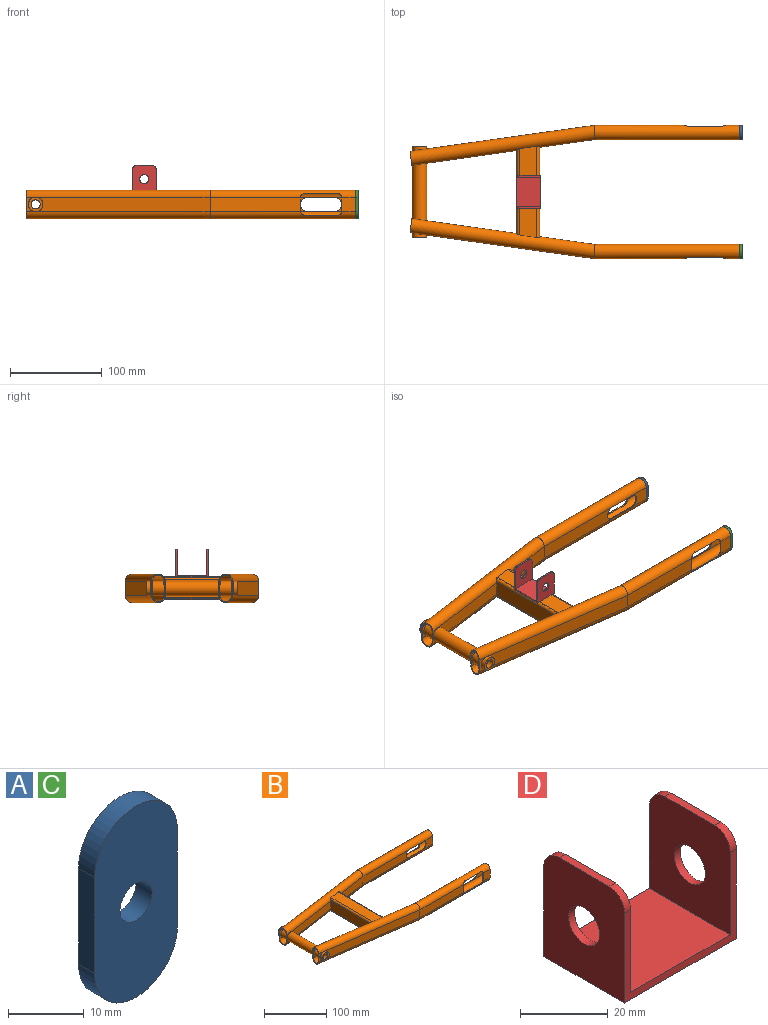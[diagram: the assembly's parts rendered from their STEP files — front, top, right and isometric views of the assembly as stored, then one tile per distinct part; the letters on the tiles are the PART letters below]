
ASSEMBLY  parts=4 mates=3
PART A: 7 faces, bbox 15.5x3x31 mm
  f0: cylinder r=7.75mm len=15.5mm, axis (0,1,0), area 73mm2, adj f1,f3,f4,f5
  f1: plane 15.5x3mm, normal (-1,0,0), area 46.5mm2, adj f0,f2,f4,f5
  f2: cylinder r=7.75mm len=15.5mm, axis (0,1,0), area 73mm2, adj f1,f3,f4,f5
  f3: plane 15.5x3mm, normal (1,0,0), area 46.5mm2, adj f0,f2,f4,f5
  f4: plane 31x15.5mm, normal (0,-1,0), area 400.7mm2, adj f0,f1,f2,f3,f6
  f5: plane 31x15.5mm, normal (0,1,0), area 400.7mm2, adj f0,f1,f2,f3,f6
  f6: cylinder r=3mm len=6mm, axis (0,-1,0), area 56.5mm2, adj f4,f5
PART B: 107 faces, bbox 359.6x145.6x31.1 mm
  f0: plane 60.41x15.5mm, normal (0.14,-0.99,0), area 945.6mm2, adj f2,f3,f19,f93
  f1: plane 60.41x15.5mm, normal (0.14,0.99,0), area 945.6mm2, adj f4,f66,f80,f93
  f2: cylinder r=7.75mm len=203.08mm, axis (-0.99,-0.14,0), area 4801.1mm2, adj f0,f5,f6,f16,f17,f20,f22,f82
  f3: cylinder r=7.75mm len=203.08mm, axis (-0.99,-0.14,0), area 4801.1mm2, adj f0,f5,f6,f16,f17,f18,f22,f82
  f4: cylinder r=7.75mm len=203.08mm, axis (-0.99,0.14,0), area 4801.1mm2, adj f1,f42,f63,f67,f68,f69,f79,f81
  f5: plane 15.5x8.5mm, normal (-0.14,0.99,0), area 63.2mm2, adj f2,f3,f22,f83
  f6: plane 15.5x6.34mm, normal (0.14,-0.99,0), area 29.4mm2, adj f2,f3,f22,f82
  f7: cylinder r=6.55mm len=202.67mm, axis (-0.99,-0.14,0), area 4162.7mm2, adj f8,f10,f22,f24,f25,f28,f41
  f8: plane 15.5x8.33mm, normal (0.14,-0.99,0), area 60.6mm2, adj f7,f9,f22,f41
  f9: cylinder r=6.55mm len=202.67mm, axis (-0.99,-0.14,0), area 4162.7mm2, adj f8,f10,f22,f24,f25,f26,f41
  f10: plane 15.5x6.51mm, normal (-0.14,0.99,0), area 32mm2, adj f7,f9,f22,f41
  f11: plane 15.5x14.85mm, normal (0,1,0), area 229.3mm2, adj f18,f20,f23,f33,f34,f35
  f12: plane 15.5x14.85mm, normal (0,-1,0), area 229.3mm2, adj f23,f26,f28,f33,f34,f35
  f13: plane 22.54x15.5mm, normal (0,-1,0), area 255mm2, adj f18,f20,f23,f29
  f14: plane 22.54x15.5mm, normal (0,1,0), area 255mm2, adj f23,f26,f28,f29
  f15: plane 105.53x15.5mm, normal (0,1,0), area 1541.4mm2, adj f25,f26,f28,f31
  f16: plane 188.46x26.49mm, normal (-0.14,0.99,0), area 2880.1mm2, adj f2,f3,f21,f83
  f17: plane 104.13x15.5mm, normal (0.14,-0.99,0), area 1560.1mm2, adj f2,f3,f82,f92
  f18: cylinder r=7.75mm len=158.57mm, axis (-1,0,0), area 3657mm2, adj f3,f11,f13,f19,f21,f23,f30,f33
  f19: plane 105.45x15.5mm, normal (0,-1,0), area 1540.1mm2, adj f0,f18,f20,f31
  f20: cylinder r=7.75mm len=158.57mm, axis (-1,0,0), area 3657mm2, adj f2,f11,f13,f19,f21,f23,f32,f35
  f21: plane 98.84x15.5mm, normal (0,1,0), area 1531.1mm2, adj f16,f18,f20,f37,f38,f39
  f22: plane 31x15.35mm, normal (-0.99,-0.14,0), area 91.1mm2, adj f2,f3,f5,f6,f7,f8,f9,f10
  f23: plane 31x15.5mm, normal (1,0,0), area 91.1mm2, adj f11,f12,f13,f14,f18,f20,f26,f28
  f24: plane 188.55x26.5mm, normal (0.14,-0.99,0), area 2881.4mm2, adj f7,f9,f27,f41
  f25: plane 189.46x26.63mm, normal (-0.14,0.99,0), area 2895.7mm2, adj f7,f9,f15,f41
  f26: cylinder r=6.55mm len=158.49mm, axis (-1,0,0), area 3056.2mm2, adj f9,f12,f14,f15,f23,f27,f30,f33
  f27: plane 98.75x15.5mm, normal (0,-1,0), area 1529.8mm2, adj f24,f26,f28,f37,f38,f39
  f28: cylinder r=6.55mm len=158.49mm, axis (-1,0,0), area 3056.2mm2, adj f7,f12,f14,f15,f23,f27,f32,f35
  f29: cylinder r=7.75mm len=15.5mm, axis (0,-1,0), area 29.2mm2, adj f13,f14,f30,f32
  f30: plane 29.5x1.2mm, normal (0,0,-1), area 35.4mm2, adj f18,f26,f29,f31
  f31: cylinder r=7.75mm len=15.5mm, axis (0,-1,0), area 29.2mm2, adj f15,f19,f30,f32
  f32: plane 29.5x1.2mm, normal (0,0,1), area 35.4mm2, adj f20,f28,f29,f31
  f33: cylinder r=5mm len=5mm, axis (0,1,0), area 10.4mm2, adj f11,f12,f18,f26,f34,f40
  f34: plane 14x1.2mm, normal (-1,0,0), area 16.8mm2, adj f11,f12,f33,f35
  f35: cylinder r=5mm len=5mm, axis (0,1,0), area 10.4mm2, adj f11,f12,f20,f28,f34,f36
  f36: plane 35x1.5mm, normal (0,0,1), area 52.4mm2, adj f20,f28,f35,f37
  f37: cylinder r=5mm len=5mm, axis (0,1,0), area 10.4mm2, adj f20,f21,f27,f28,f36,f38
  f38: plane 14x1.2mm, normal (1,0,0), area 16.8mm2, adj f21,f27,f37,f39
  f39: cylinder r=5mm len=5mm, axis (0,1,0), area 10.4mm2, adj f18,f21,f26,f27,f38,f40
  f40: plane 35x1.5mm, normal (0,0,-1), area 52.4mm2, adj f18,f26,f33,f39
  f41: cylinder r=8mm len=16mm, axis (0,1,0), area 664.9mm2, adj f7,f8,f9,f10,f24,f25
  f42: cylinder r=8mm len=16mm, axis (0,1,0), area 201.8mm2, adj f4,f43,f69,f80,f81
  f43: plane 16x16mm, normal (0,-1,0), area 122.5mm2, adj f42,f85
  f44: cylinder r=8mm len=16mm, axis (0,1,0), area 664.9mm2, adj f60,f61,f75,f76,f77,f78
  f45: plane 35x1.5mm, normal (0,0,-1), area 52.4mm2, adj f46,f52,f59,f67
  f46: cylinder r=5mm len=5mm, axis (0,-1,0), area 10.4mm2, adj f45,f47,f58,f59,f64,f67
  f47: plane 14x1.2mm, normal (1,0,0), area 16.8mm2, adj f46,f48,f58,f64
  f48: cylinder r=5mm len=5mm, axis (0,-1,0), area 10.4mm2, adj f47,f49,f57,f58,f64,f65
  f49: plane 35x1.5mm, normal (0,0,1), area 52.4mm2, adj f48,f50,f57,f65
  f50: cylinder r=5mm len=5mm, axis (0,-1,0), area 10.4mm2, adj f49,f51,f57,f65,f73,f74
  f51: plane 14x1.2mm, normal (-1,0,0), area 16.8mm2, adj f50,f52,f73,f74
  f52: cylinder r=5mm len=5mm, axis (0,-1,0), area 10.4mm2, adj f45,f51,f59,f67,f73,f74
  f53: plane 29.5x1.2mm, normal (0,0,1), area 35.4mm2, adj f54,f56,f57,f65
  f54: cylinder r=7.75mm len=15.5mm, axis (0,1,0), area 29.2mm2, adj f53,f55,f66,f70
  f55: plane 29.5x1.2mm, normal (0,0,-1), area 35.4mm2, adj f54,f56,f59,f67
  f56: cylinder r=7.75mm len=15.5mm, axis (0,1,0), area 29.2mm2, adj f53,f55,f71,f72
  f57: cylinder r=6.55mm len=158.49mm, axis (-1,0,0), area 3056.2mm2, adj f48,f49,f50,f53,f58,f62,f70,f71
  f58: plane 98.75x15.5mm, normal (0,1,0), area 1529.8mm2, adj f46,f47,f48,f57,f59,f77
  f59: cylinder r=6.55mm len=158.49mm, axis (-1,0,0), area 3056.2mm2, adj f45,f46,f52,f55,f58,f62,f70,f71
  f60: plane 15.5x6.51mm, normal (-0.14,-0.99,0), area 32mm2, adj f44,f63,f76,f78
  f61: plane 15.5x8.33mm, normal (0.14,0.99,0), area 60.6mm2, adj f44,f63,f76,f78
  f62: plane 31x15.5mm, normal (1,0,0), area 91.1mm2, adj f57,f59,f65,f67,f71,f72,f73,f74
  f63: plane 31x15.35mm, normal (-0.99,0.14,0), area 91.1mm2, adj f4,f60,f61,f68,f69,f76,f78,f80
  f64: plane 98.84x15.5mm, normal (0,-1,0), area 1531.1mm2, adj f46,f47,f48,f65,f67,f81
  f65: cylinder r=7.75mm len=158.57mm, axis (-1,0,0), area 3657mm2, adj f48,f49,f50,f53,f62,f64,f66,f72
  f66: plane 105.45x15.5mm, normal (0,1,0), area 1540.1mm2, adj f1,f54,f65,f67
  f67: cylinder r=7.75mm len=158.57mm, axis (-1,0,0), area 3657mm2, adj f4,f45,f46,f52,f55,f62,f64,f66
  f68: plane 15.5x6.34mm, normal (0.14,0.99,0), area 29.4mm2, adj f4,f63,f80,f82
  f69: plane 15.5x8.5mm, normal (-0.14,-0.99,0), area 63.2mm2, adj f4,f42,f63,f80
  f70: plane 105.53x15.5mm, normal (0,-1,0), area 1541.4mm2, adj f54,f57,f59,f75
  f71: plane 22.54x15.5mm, normal (0,-1,0), area 255mm2, adj f56,f57,f59,f62
  f72: plane 22.54x15.5mm, normal (0,1,0), area 255mm2, adj f56,f62,f65,f67
  f73: plane 15.5x14.85mm, normal (0,1,0), area 229.3mm2, adj f50,f51,f52,f57,f59,f62
  f74: plane 15.5x14.85mm, normal (0,-1,0), area 229.3mm2, adj f50,f51,f52,f62,f65,f67
  f75: plane 189.46x26.63mm, normal (-0.14,-0.99,0), area 2895.7mm2, adj f44,f70,f76,f78
  f76: cylinder r=6.55mm len=202.67mm, axis (-0.99,0.14,0), area 4162.7mm2, adj f44,f59,f60,f61,f63,f75,f77
  f77: plane 188.55x26.5mm, normal (0.14,0.99,0), area 2881.4mm2, adj f44,f58,f76,f78
  f78: cylinder r=6.55mm len=202.67mm, axis (-0.99,0.14,0), area 4162.7mm2, adj f44,f57,f60,f61,f63,f75,f77
  f79: plane 104.13x15.5mm, normal (0.14,0.99,0), area 1560.1mm2, adj f4,f80,f82,f92
  f80: cylinder r=7.75mm len=203.08mm, axis (-0.99,0.14,0), area 4801.1mm2, adj f1,f42,f63,f65,f68,f69,f79,f81
  f81: plane 188.46x26.49mm, normal (-0.14,-0.99,0), area 2880.1mm2, adj f4,f42,f64,f80
  f82: cylinder r=8mm len=62.92mm, axis (0,1,0), area 3049.3mm2, adj f2,f3,f4,f6,f17,f68,f79,f80
  f83: cylinder r=8mm len=16mm, axis (0,1,0), area 201.8mm2, adj f2,f3,f5,f16,f84
  f84: plane 16x16mm, normal (0,1,0), area 122.5mm2, adj f83,f85
  f85: cylinder r=5mm len=100mm, axis (0,-1,0), area 3141.6mm2, adj f43,f84
  f86: cylinder r=3mm len=100.04mm, axis (0,1,0), area 467.6mm2, adj f3,f4,f88,f93
  f87: cylinder r=3mm len=94.62mm, axis (0,1,0), area 437.4mm2, adj f3,f4,f88,f92
  f88: plane 99.96x19mm, normal (0,0,1), area 1848.5mm2, adj f3,f4,f86,f87
  f89: cylinder r=3mm len=94.62mm, axis (0,1,0), area 437.4mm2, adj f2,f80,f91,f92
  f90: cylinder r=3mm len=100.04mm, axis (0,1,0), area 467.6mm2, adj f2,f80,f91,f93
  f91: plane 99.96x19mm, normal (0,0,-1), area 1848.5mm2, adj f2,f80,f89,f90
  f92: plane 90.91x19.01mm, normal (-1,0,0), area 1719.8mm2, adj f2,f3,f4,f17,f79,f80,f87,f89
  f93: plane 97.94x19.01mm, normal (1,0,0), area 1853.3mm2, adj f0,f1,f2,f3,f4,f80,f86,f90
  f94: plane 97.91x20.02mm, normal (-1,0,0), area 1945.2mm2, adj f98,f99,f101,f102,f103,f104,f105,f106
  f95: plane 98.66x20mm, normal (0,0,-1), area 1917mm2, adj f98,f100,f101,f105
  f96: plane 98.66x21.4mm, normal (0,0,1), area 2047mm2, adj f97,f99,f102,f104
  f97: plane 92.71x21.46mm, normal (1,0,0), area 1945.8mm2, adj f96,f100,f101,f102,f103,f104,f105,f106
  f98: cylinder r=1.4mm len=98.71mm, axis (0,1,0), area 216.5mm2, adj f94,f95,f101,f105
  f99: cylinder r=1.4mm len=98.71mm, axis (0,1,0), area 216.5mm2, adj f94,f96,f102,f104
  f100: cylinder r=1.4mm len=93.04mm, axis (0,1,0), area 203mm2, adj f95,f97,f101,f105
  f101: cylinder r=7.75mm len=22.98mm, axis (-0.99,0.14,0), area 86.6mm2, adj f94,f95,f97,f98,f100,f103
  f102: cylinder r=7.75mm len=22.98mm, axis (-0.99,0.14,0), area 87mm2, adj f94,f96,f97,f99,f103
  f103: plane 22.8x15.5mm, normal (0.14,0.99,0), area 356.9mm2, adj f94,f97,f101,f102
  f104: cylinder r=7.75mm len=22.98mm, axis (-0.99,-0.14,0), area 87mm2, adj f94,f96,f97,f99,f106
  f105: cylinder r=7.75mm len=22.98mm, axis (-0.99,-0.14,0), area 86.6mm2, adj f94,f95,f97,f98,f100,f106
  f106: plane 22.8x15.5mm, normal (0.14,-0.99,0), area 356.9mm2, adj f94,f97,f104,f105
PART C: same geometry as A
PART D: 16 faces, bbox 36x26x30 mm
  f0: plane 16x2mm, normal (0,0,1), area 32mm2, adj f1,f7,f11,f13
  f1: plane 30x26mm, normal (-1,0,0), area 690.7mm2, adj f0,f2,f8,f9,f11,f13,f14
  f2: plane 36x26mm, normal (0,0,-1), area 936mm2, adj f1,f3,f8,f9
  f3: plane 30x26mm, normal (1,0,0), area 690.7mm2, adj f2,f4,f8,f9,f10,f12,f15
  f4: plane 16x2mm, normal (0,0,1), area 32mm2, adj f3,f5,f10,f12
  f5: plane 28x26mm, normal (-1,0,0), area 638.7mm2, adj f4,f6,f8,f9,f10,f12,f15
  f6: plane 32x26mm, normal (0,0,1), area 832mm2, adj f5,f7,f8,f9
  f7: plane 28x26mm, normal (1,0,0), area 638.7mm2, adj f0,f6,f8,f9,f11,f13,f14
  f8: plane 36x25mm, normal (0,-1,0), area 164mm2, adj f1,f2,f3,f5,f6,f7,f12,f13
  f9: plane 36x25mm, normal (0,1,0), area 164mm2, adj f1,f2,f3,f5,f6,f7,f10,f11
  f10: cylinder r=5mm len=5mm, axis (-1,0,0), area 15.7mm2, adj f3,f4,f5,f9
  f11: cylinder r=5mm len=5mm, axis (-1,0,0), area 15.7mm2, adj f0,f1,f7,f9
  f12: cylinder r=5mm len=5mm, axis (1,0,0), area 15.7mm2, adj f3,f4,f5,f8
  f13: cylinder r=5mm len=5mm, axis (1,0,0), area 15.7mm2, adj f0,f1,f7,f8
  f14: cylinder r=5mm len=10mm, axis (-1,0,0), area 62.8mm2, adj f1,f7
  f15: cylinder r=5mm len=10mm, axis (-1,0,0), area 62.8mm2, adj f3,f5
PLACE A rot(axis=(0,0,-1),90deg) t=(30.93,-2.12,30.8)mm
PLACE B t=(27.93,-67.12,30.8)mm fixed
PLACE C rot(axis=(0,0,-1),90deg) t=(30.93,-132.12,30.8)mm
PLACE D rot(axis=(0,0,1),90deg) t=(-215.39,-67.12,58.3)mm
MATE fastened B.f88 <-> D.f2  axis (0,0,1) through (-202.39,-67.12,43.3)mm
MATE fastened A.f0 <-> B.f18  axis (-1,0,0) through (27.93,-2.12,38.55)mm
MATE fastened C.f0 <-> B.f59  axis (-1,0,0) through (27.93,-132.12,38.55)mm
